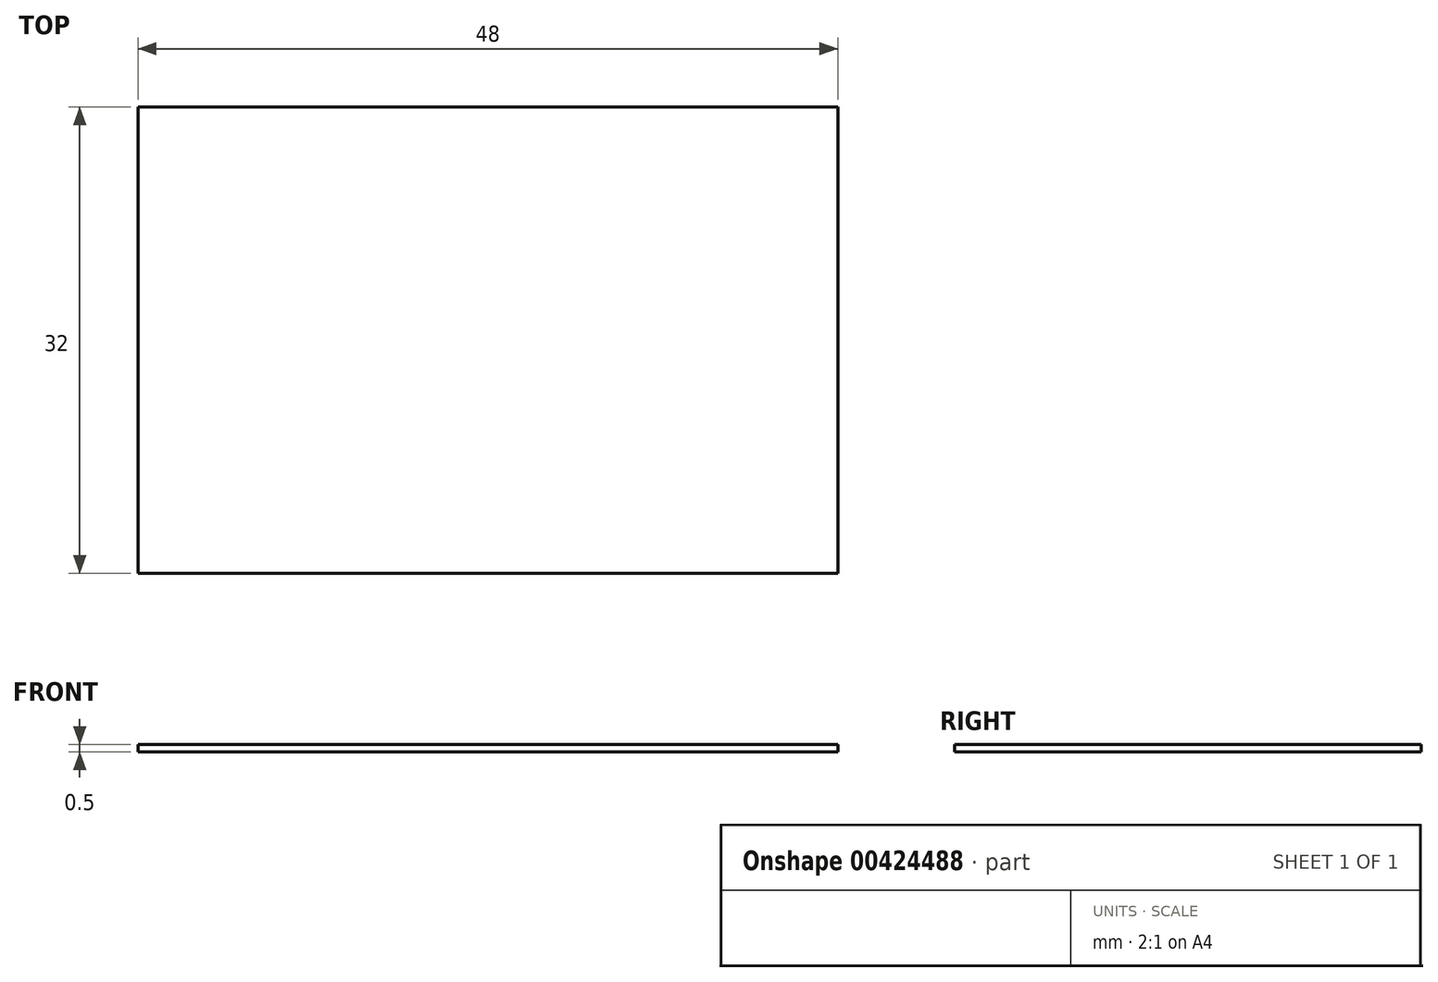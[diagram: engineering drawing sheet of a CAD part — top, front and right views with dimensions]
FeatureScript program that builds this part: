
annotation { "Feature Type Name" : "Feature", "Feature Type Description" : "" }
export const myFeature = defineFeature(function(context is Context, id is Id, definition is map)
    precondition{}
    {
        {
            var Q0;
            Q0=qCreatedBy(makeId("Top.planeOp"),FACE);
            var sketch = newSketch(context, id + "F0", { "sketchPlane" : qUnion([Q0])});
            skLineSegment(sketch, "E0.bottom", {"start": v(24, 16) * mm, "end": v(-24, 16) * mm});
            skLineSegment(sketch, "E0.top", {"start": v(24, -16) * mm, "end": v(-24, -16) * mm});
            skLineSegment(sketch, "E0.left", {"start": v(24, 16) * mm, "end": v(24, -16) * mm});
            skLineSegment(sketch, "E0.right", {"start": v(-24, 16) * mm, "end": v(-24, -16) * mm});
            skPoint(sketch, "E0.middle", {"position": v(0, 0) * mm});
            skSolve(sketch);
        }
        {
            var Q0;
            Q0=makeQuery(id+"F0.imprint","IMPRINT",FACE,{"disambiguationData":[TD([[makeQuery(id+"F0.imprint","IMPRINT",EDGE,{"derivedFrom":sQuery(id+"F0.wireOp",EDGE,"E0.bottom")}),1.0]])]});
            extrude(context, id + "F1", {"entities" : qUnion([Q0]), "depth" : .5 * mm});
        }
    });
